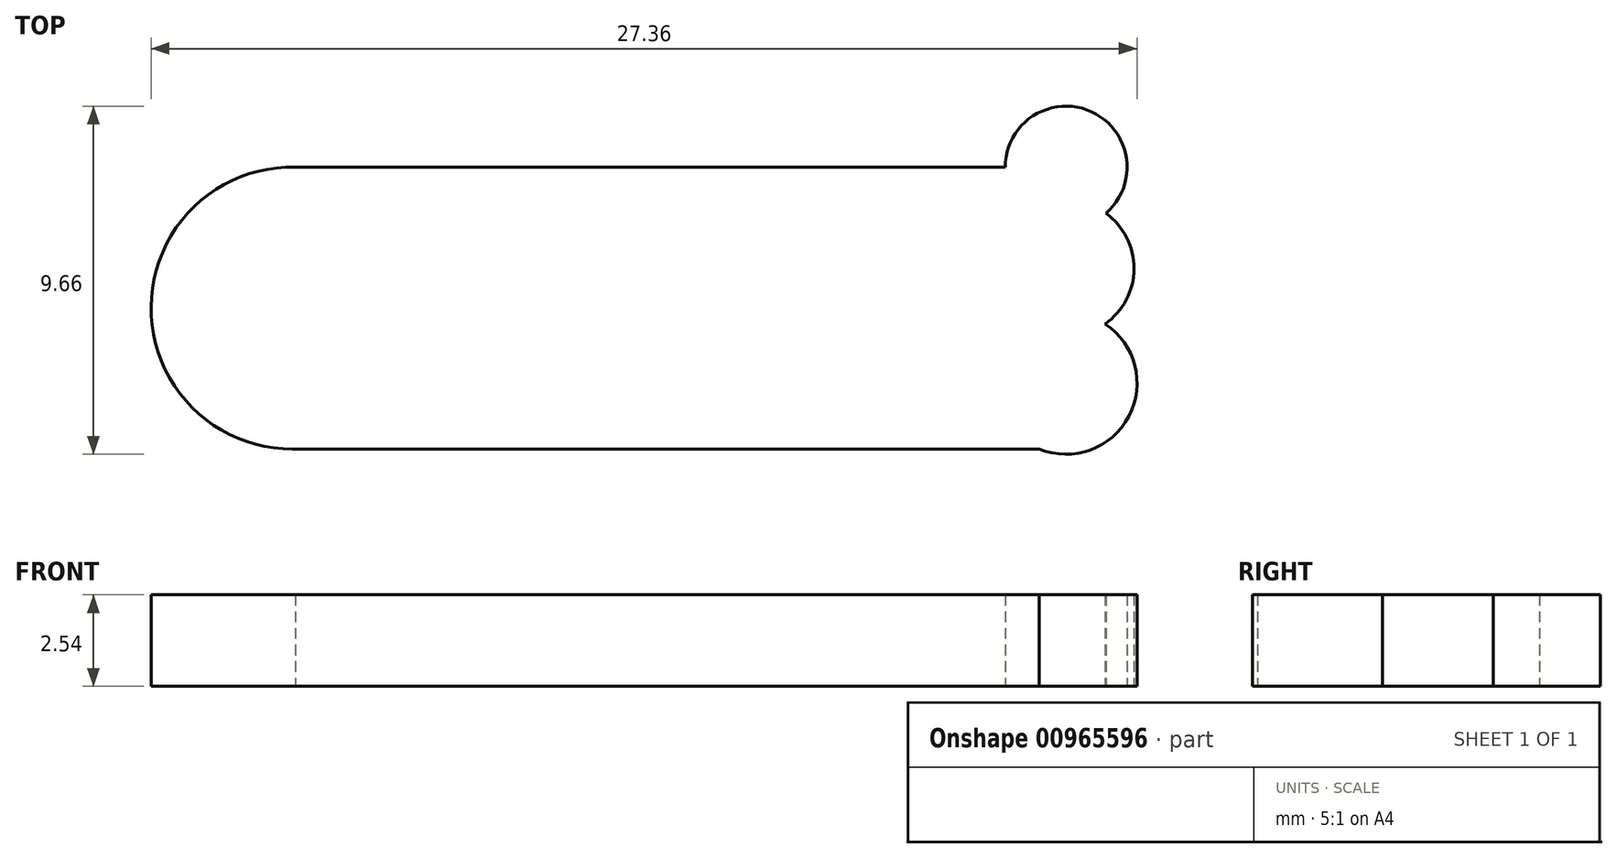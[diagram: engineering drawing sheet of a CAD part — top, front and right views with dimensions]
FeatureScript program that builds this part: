
annotation { "Feature Type Name" : "Feature", "Feature Type Description" : "" }
export const myFeature = defineFeature(function(context is Context, id is Id, definition is map)
    precondition{}
    {
        {
            var Q0;
            Q0=qCreatedBy(makeId("Top.planeOp"),FACE);
            var sketch = newSketch(context, id + "F0", { "sketchPlane" : qUnion([Q0])});
            skCircle(sketch, "E0", {"center": v(-48.22, 27.86) * mm, "radius": 3.91 * mm});
            skLineSegment(sketch, "E1", {"start": v(-48.12, 31.77) * mm, "end": v(-26.74, 31.77) * mm});
            skLineSegment(sketch, "E2", {"start": v(-48.2, 23.95) * mm, "end": v(-26.32, 23.95) * mm});
            skCircle(sketch, "E3", {"center": v(-26.74, 31.77) * mm, "radius": 1.7 * mm});
            skCircle(sketch, "E4", {"center": v(-26.74, 28.96) * mm, "radius": 1.88 * mm});
            skCircle(sketch, "E5", {"center": v(-26.74, 25.77) * mm, "radius": 1.97 * mm});
            skSolve(sketch);
        }
        {
            var Q0;
            Q0 = qSketchRegion(id + "F0", true);
            extrude(context, id + "F1", {"entities" : qUnion([Q0]), "depth" : 2.54 * mm, "offsetDistance" : 25.4 * mm});
        }
    });
